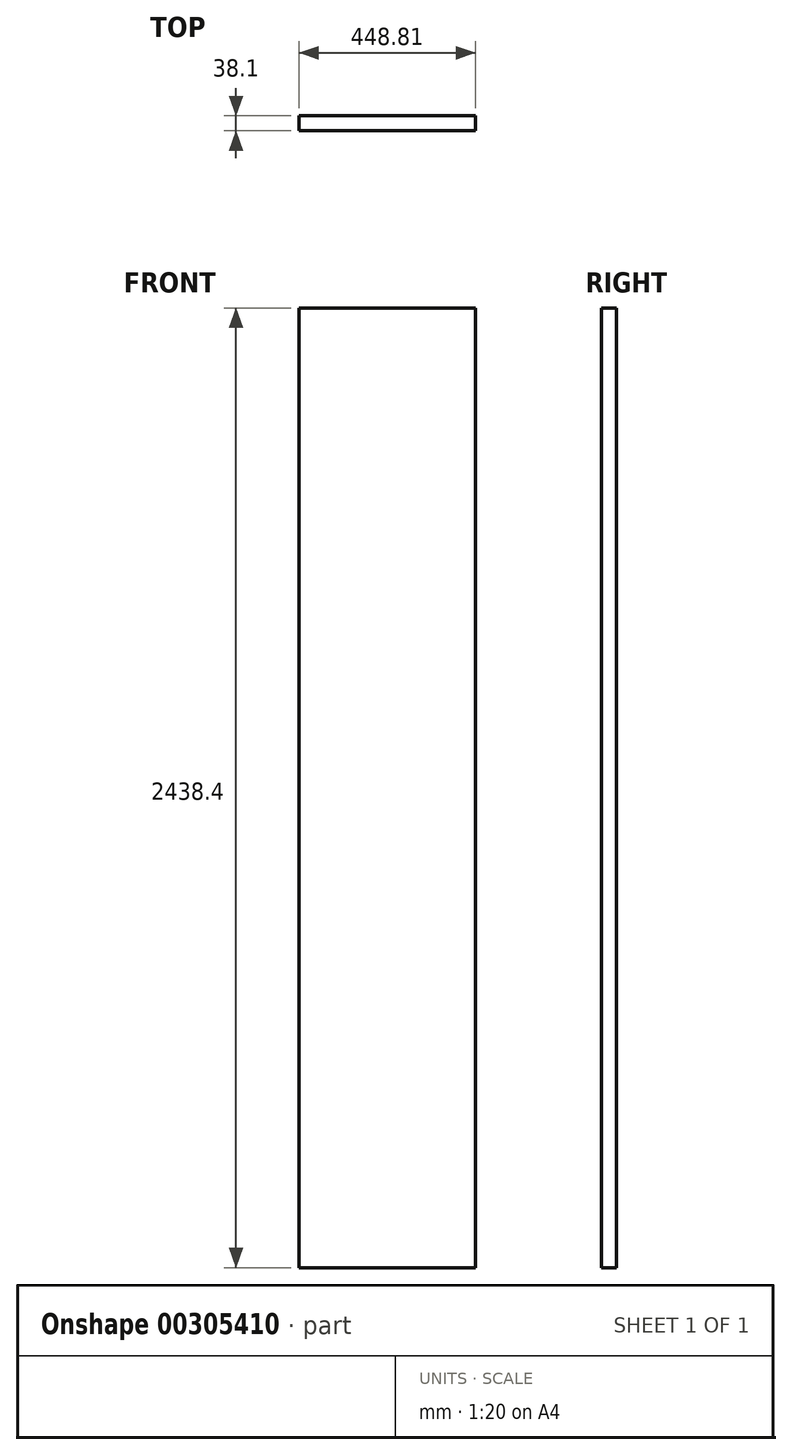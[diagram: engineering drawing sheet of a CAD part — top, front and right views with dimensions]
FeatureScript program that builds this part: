
annotation { "Feature Type Name" : "Feature", "Feature Type Description" : "" }
export const myFeature = defineFeature(function(context is Context, id is Id, definition is map)
    precondition{}
    {
        {
            var Q0;
            Q0=qCreatedBy(makeId("Top.planeOp"),FACE);
            var sketch = newSketch(context, id + "F0", { "sketchPlane" : qUnion([Q0])});
            skLineSegment(sketch, "E0.bottom", {"start": v(-227.31, 3.73) * mm, "end": v(221.5, 3.73) * mm});
            skLineSegment(sketch, "E0.top", {"start": v(-227.31, -34.37) * mm, "end": v(221.5, -34.37) * mm});
            skLineSegment(sketch, "E0.left", {"start": v(-227.31, 3.73) * mm, "end": v(-227.31, -34.37) * mm});
            skLineSegment(sketch, "E0.right", {"start": v(221.5, 3.73) * mm, "end": v(221.5, -34.37) * mm});
            skSolve(sketch);
        }
        {
            var Q0;
            Q0=makeQuery(id+"F0.imprint","IMPRINT",FACE,{"disambiguationData":[TD([[makeQuery(id+"F0.imprint","IMPRINT",EDGE,{"derivedFrom":sQuery(id+"F0.wireOp",EDGE,"E0.bottom")}),-1.0]])]});
            extrude(context, id + "F1", {"entities" : qUnion([Q0]), "depth" : 2438.4 * mm});
        }
    });
